# Revit family: Differential Pressure Control Valve F 4007 50-150 HT Distric heating type, supplyreturn
name_source: partatom
category: Rohrzubehör
revit_build: Autodesk Revit 2018 (Build: 20190510_1515(x64)
units: mm (PartAtom-declared; Revit-internal decimal feet)

## family parameters
Arbeitsebenenbasiert = Nein
Beim Laden mit Abzugskörper schneiden = Nein
Bemaßung runder Anschluss = Durchmesser verwenden
Gemeinsam genutzt = Nein
Immer vertikal = Ja
OmniClass-Nummer = 23.65.55.14
OmniClass-Titel = Valves for Liquid Services
Teiletyp = Unterbricht

## types (1)
- Differential Pressure Control Valve F 4007 50-150 HT Distric heating type, supplyreturn
    Application = For heating and cooling systems, to ensure constant differential pressure within the control range.
    Body = EN-GJL-250 gem. EN 1561
    D03 = 21 mm  [stored 0.0688976 ft]
    D07 = 30 mm
    D08 = 24 mm  [stored 0.0787402 ft]
    D14 = 50 mm  [stored 0.164042 ft]
    D15 = 35 mm  [stored 0.114829 ft]
    D16 = 45 mm  [stored 0.147638 ft]
    D17 = 6 mm  [stored 0.019685 ft]
    Diaphragm = EPDM with textile
    Differential pressure setting range = 50-150 kPa
    H04 = 5 mm  [stored 0.0164042 ft]
    H05 = 3 mm  [stored 0.00984252 ft]
    H08 = 21 mm  [stored 0.0688976 ft]
    H10 = 5 mm  [stored 0.0164042 ft]
    H13 = 17 mm
    H14 = 5 mm  [stored 0.0164042 ft]
    H15 = 25 mm  [stored 0.082021 ft]
    H16 = 10 mm  [stored 0.0328084 ft]
    H17 = 6 mm  [stored 0.019685 ft]
    Hersteller = HERZ Armaturen Ges.m.b.H.
    L01 = 3 mm  [stored 0.00984252 ft]
    L03 = 10 mm  [stored 0.0328084 ft]
    Max. differential pressure = 400000.0 Pa
    Max. operating pressure = 1600000.0 Pa
    Max. operating temperature = 150 °C
    Medium = Water purity in accordance with ÖNORM H 5195 and VDI 2035 standards.
Ethylene and propylene glycol can be mixed in ratio of 25 - 50 vol. [%].
    Min. operating temperature = 2 °C
    Min. operating temperature (anti freeze) = -10 °C
    Model = The differential pressure controller is a straight-version proportional controller and works without auxiliary energy.
The required nominal differential pressure can be continuously adjusted from 50 to 150 kPa.
The impulse pipe (1500 mm) is included in the valve set and has to be connected to a double regulating valve on the supply side.
    O-Ring = EPDM
    R02 = 16 mm
    R97 = 2 mm  [stored 0.00656168 ft]
    R98 = 6 mm  [stored 0.019685 ft]
    R99 = 14 mm  [stored 0.0459318 ft]
    SCRNCODE = 05;03;02
    SCRNSEQ = ARM;ARM_TYP="DIFR";2
    Spring = EN 10270-1-SH
    Testing pressure = 2500000.0 Pa
    Type of connection = EN 1092-2
    URL = www.herzvalves.com

note: [stored X ft] marks values corroborated as IEEE doubles in the binary element streams (Revit-internal decimal feet)
